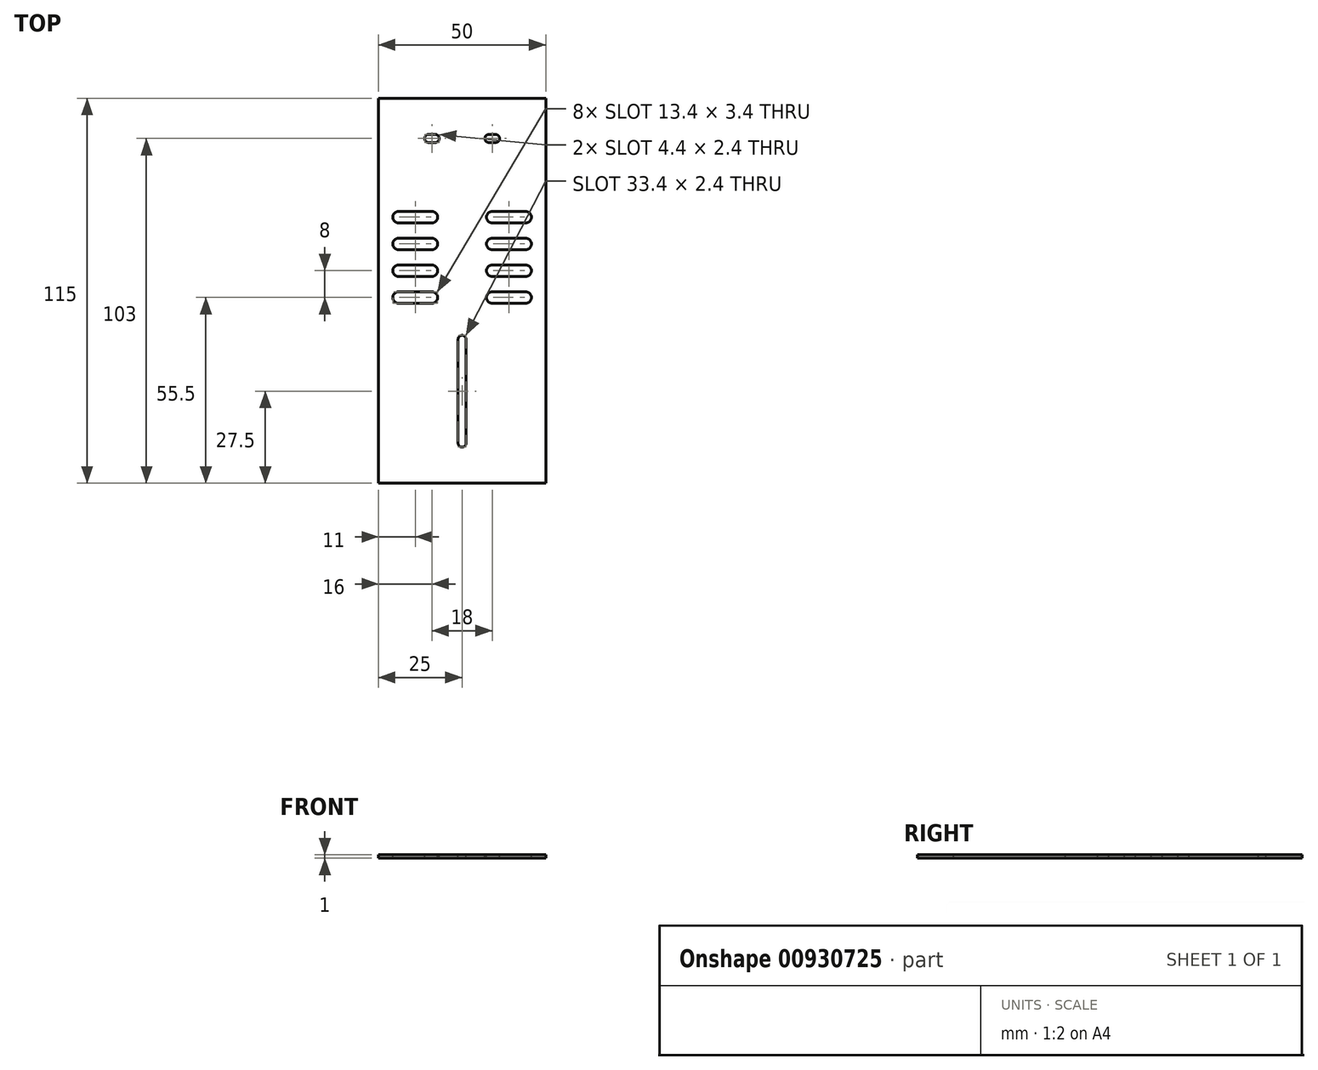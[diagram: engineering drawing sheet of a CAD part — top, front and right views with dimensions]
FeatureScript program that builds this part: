
annotation { "Feature Type Name" : "Feature", "Feature Type Description" : "" }
export const myFeature = defineFeature(function(context is Context, id is Id, definition is map)
    precondition{}
    {
        {
            var Q0;
            Q0=qCreatedBy(makeId("Top.planeOp"),FACE);
            var sketch = newSketch(context, id + "F0", { "sketchPlane" : qUnion([Q0])});
            skLineSegment(sketch, "E0", {"start": v(0, 12) * mm, "end": v(-25, 12) * mm});
            skLineSegment(sketch, "E1", {"start": v(-25, 12) * mm, "end": v(-25, -103) * mm});
            skLineSegment(sketch, "E2", {"start": v(0, 12) * mm, "end": v(25, 12) * mm});
            skLineSegment(sketch, "E3", {"start": v(-25, -103) * mm, "end": v(25, -103) * mm});
            skArc(sketch, "E4", {"start": v(-1.2, -91) * mm, "mid": v(0, -92.2) * mm, "end": v(1.2, -91) * mm});
            skArc(sketch, "E5", {"start": v(1.2, -60) * mm, "mid": v(0, -58.8) * mm, "end": v(-1.2, -60) * mm});
            skArc(sketch, "E6", {"start": v(-10, 1.2) * mm, "mid": v(-11.2, 0) * mm, "end": v(-10, -1.2) * mm});
            skLineSegment(sketch, "E7", {"start": v(-8, 1.2) * mm, "end": v(-10, 1.2) * mm});
            skArc(sketch, "E8.trimOffspring", {"start": v(-8, -1.2) * mm, "mid": v(-6.8, 0) * mm, "end": v(-8, 1.2) * mm});
            skArc(sketch, "E9", {"start": v(10, -1.2) * mm, "mid": v(11.2, 0) * mm, "end": v(10, 1.2) * mm});
            skLineSegment(sketch, "E10", {"start": v(10, -1.2) * mm, "end": v(8, -1.2) * mm});
            skArc(sketch, "E11", {"start": v(8, 1.2) * mm, "mid": v(6.8, 0) * mm, "end": v(8, -1.2) * mm});
            skLineSegment(sketch, "E12", {"start": v(10, 1.2) * mm, "end": v(8, 1.2) * mm});
            skLineSegment(sketch, "E13", {"start": v(-10, -1.2) * mm, "end": v(-8, -1.2) * mm});
            skLineSegment(sketch, "E14", {"start": v(1.2, -60) * mm, "end": v(1.2, -91) * mm});
            skLineSegment(sketch, "E15", {"start": v(-1.2, -60) * mm, "end": v(-1.2, -91) * mm});
            skLineSegment(sketch, "E16", {"start": v(0, -91) * mm, "end": v(0, -79.5) * mm, "construction": true});
            skPoint(sketch, "E17.orphan", {"position": v(25, -63.5) * mm});
            skPoint(sketch, "E18.orphan", {"position": v(-25, -55.5) * mm});
            skPoint(sketch, "E19.orphan", {"position": v(25, -55.5) * mm});
            skPoint(sketch, "E20.end.orphan", {"position": v(0, -55.5) * mm});
            skLineSegment(sketch, "E21", {"start": v(19, -49.2) * mm, "end": v(9, -49.2) * mm});
            skLineSegment(sketch, "E22", {"start": v(19, -45.8) * mm, "end": v(9, -45.8) * mm});
            skArc(sketch, "E23", {"start": v(19, -49.2) * mm, "mid": v(20.7, -47.5) * mm, "end": v(19, -45.8) * mm});
            skArc(sketch, "E24", {"start": v(9, -45.8) * mm, "mid": v(7.3, -47.5) * mm, "end": v(9, -49.2) * mm});
            skPoint(sketch, "E25.11.0.2.end.orphan", {"position": v(19, -53.8) * mm});
            skPoint(sketch, "E26.end.orphan", {"position": v(19, -57.2) * mm});
            skPoint(sketch, "E27.center.orphan", {"position": v(6, -55.5) * mm});
            skPoint(sketch, "E27.end.orphan", {"position": v(6, -57.2) * mm});
            skLineSegment(sketch, "E28", {"start": v(25, 12) * mm, "end": v(25, -103) * mm});
            skArc(sketch, "E29.0.1.0", {"start": v(9, -37.8) * mm, "mid": v(7.3, -39.5) * mm, "end": v(9, -41.2) * mm});
            skArc(sketch, "E29.0.1.1", {"start": v(19, -41.2) * mm, "mid": v(20.7, -39.5) * mm, "end": v(19, -37.8) * mm});
            skLineSegment(sketch, "E29.0.1.2", {"start": v(19, -37.8) * mm, "end": v(9, -37.8) * mm});
            skLineSegment(sketch, "E29.0.1.3", {"start": v(19, -41.2) * mm, "end": v(9, -41.2) * mm});
            skArc(sketch, "E29.0.2.0", {"start": v(9, -29.8) * mm, "mid": v(7.3, -31.5) * mm, "end": v(9, -33.2) * mm});
            skArc(sketch, "E29.0.2.1", {"start": v(19, -33.2) * mm, "mid": v(20.7, -31.5) * mm, "end": v(19, -29.8) * mm});
            skLineSegment(sketch, "E29.0.2.2", {"start": v(19, -29.8) * mm, "end": v(9, -29.8) * mm});
            skLineSegment(sketch, "E29.0.2.3", {"start": v(19, -33.2) * mm, "end": v(9, -33.2) * mm});
            skArc(sketch, "E29.0.3.0", {"start": v(9, -21.8) * mm, "mid": v(7.3, -23.5) * mm, "end": v(9, -25.2) * mm});
            skArc(sketch, "E29.0.3.1", {"start": v(19, -25.2) * mm, "mid": v(20.7, -23.5) * mm, "end": v(19, -21.8) * mm});
            skLineSegment(sketch, "E29.0.3.2", {"start": v(19, -21.8) * mm, "end": v(9, -21.8) * mm});
            skLineSegment(sketch, "E29.0.3.3", {"start": v(19, -25.2) * mm, "end": v(9, -25.2) * mm});
            skArc(sketch, "E29.1.0.0", {"start": v(-19, -45.8) * mm, "mid": v(-20.7, -47.5) * mm, "end": v(-19, -49.2) * mm});
            skArc(sketch, "E29.1.0.1", {"start": v(-9, -49.2) * mm, "mid": v(-7.3, -47.5) * mm, "end": v(-9, -45.8) * mm});
            skLineSegment(sketch, "E29.1.0.2", {"start": v(-9, -45.8) * mm, "end": v(-19, -45.8) * mm});
            skLineSegment(sketch, "E29.1.0.3", {"start": v(-9, -49.2) * mm, "end": v(-19, -49.2) * mm});
            skArc(sketch, "E29.1.1.0", {"start": v(-19, -37.8) * mm, "mid": v(-20.7, -39.5) * mm, "end": v(-19, -41.2) * mm});
            skArc(sketch, "E29.1.1.1", {"start": v(-9, -41.2) * mm, "mid": v(-7.3, -39.5) * mm, "end": v(-9, -37.8) * mm});
            skLineSegment(sketch, "E29.1.1.2", {"start": v(-9, -37.8) * mm, "end": v(-19, -37.8) * mm});
            skLineSegment(sketch, "E29.1.1.3", {"start": v(-9, -41.2) * mm, "end": v(-19, -41.2) * mm});
            skArc(sketch, "E29.1.2.0", {"start": v(-19, -29.8) * mm, "mid": v(-20.7, -31.5) * mm, "end": v(-19, -33.2) * mm});
            skArc(sketch, "E29.1.2.1", {"start": v(-9, -33.2) * mm, "mid": v(-7.3, -31.5) * mm, "end": v(-9, -29.8) * mm});
            skLineSegment(sketch, "E29.1.2.2", {"start": v(-9, -29.8) * mm, "end": v(-19, -29.8) * mm});
            skLineSegment(sketch, "E29.1.2.3", {"start": v(-9, -33.2) * mm, "end": v(-19, -33.2) * mm});
            skArc(sketch, "E29.1.3.0", {"start": v(-19, -21.8) * mm, "mid": v(-20.7, -23.5) * mm, "end": v(-19, -25.2) * mm});
            skArc(sketch, "E29.1.3.1", {"start": v(-9, -25.2) * mm, "mid": v(-7.3, -23.5) * mm, "end": v(-9, -21.8) * mm});
            skLineSegment(sketch, "E29.1.3.2", {"start": v(-9, -21.8) * mm, "end": v(-19, -21.8) * mm});
            skLineSegment(sketch, "E29.1.3.3", {"start": v(-9, -25.2) * mm, "end": v(-19, -25.2) * mm});
            skLineSegment(sketch, "E29.direction1", {"start": v(9, -49.2) * mm, "end": v(-19, -49.2) * mm, "construction": true});
            skLineSegment(sketch, "E29.direction2", {"start": v(9, -49.2) * mm, "end": v(9, -41.2) * mm, "construction": true});
            skSolve(sketch);
        }
        {
            var Q0;
            Q0=makeQuery(id+"F0.imprint","IMPRINT",FACE,{"disambiguationData":[TD([[makeQuery(id+"F0.imprint","IMPRINT",EDGE,{"derivedFrom":sQuery(id+"F0.wireOp",EDGE,"E0")}),1.0]])]});
            extrude(context, id + "F1", {"entities" : qUnion([Q0]), "oppositeDirection" : true, "depth" : 1 * mm, "offsetDistance" : 25 * mm});
        }
    });
